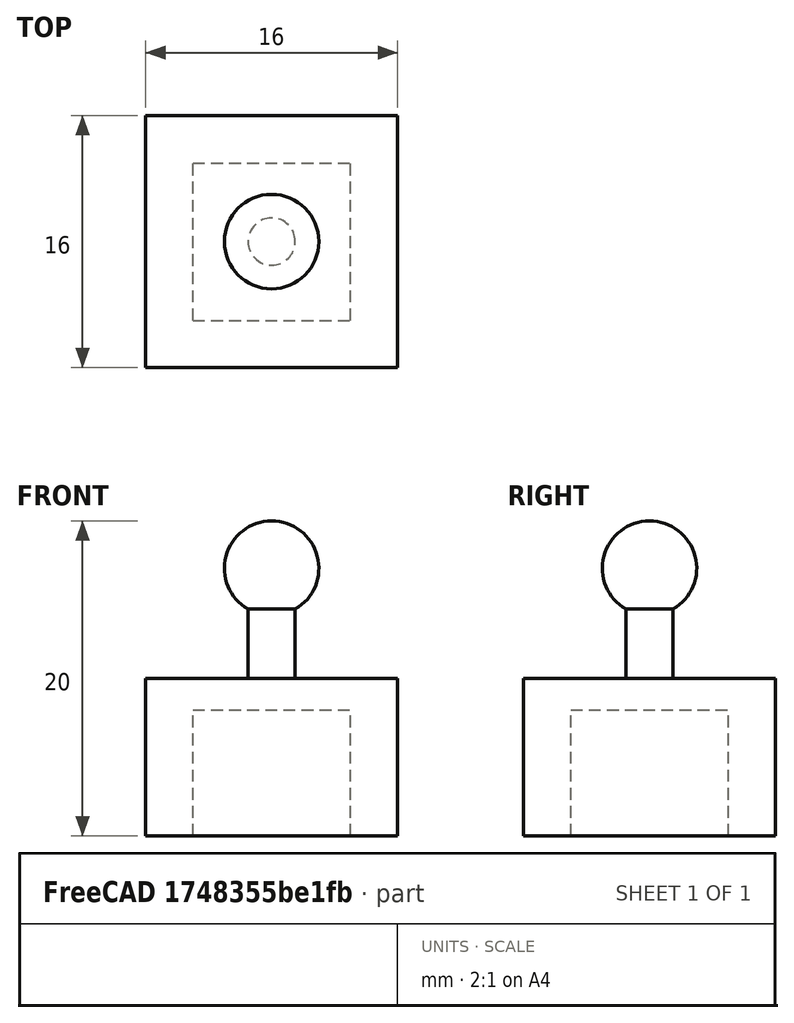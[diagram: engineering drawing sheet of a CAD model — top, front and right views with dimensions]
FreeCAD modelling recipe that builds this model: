
FCSTD DOCUMENT  (FreeCAD 0.18.3R)
Label: sphere
License: All rights reserved
LicenseURL: http://en.wikipedia.org/wiki/All_rights_reserved
objects: Part::Box×2, Part::Cylinder×1, Part::Sphere×1, Part::MultiFuse×1, Part::Cut×1
note: 6 computed .brp shape members not serialized (recipe doc carries the construction recipe); baked Part::Feature solids carry a one-line shape summary decoded from their .brp

FEATURE [Part::Box] Box  label="Cube"
  AttacherType = Attacher::AttachEngine3D
  Height = 10
  Length = 16
  Placement = pos=(-8,-8,0) rot=(0,0,1;0rad)
  Width = 16
FEATURE [Part::Cylinder] Cylinder
  Angle = 360
  AttacherType = Attacher::AttachEngine3D
  Height = 5
  Placement = pos=(0,0,10) rot=(0,0,1;0rad)
  Radius = 1.5
FEATURE [Part::Sphere] Sphere
  Angle1 = -90
  Angle2 = 90
  Angle3 = 360
  AttacherType = Attacher::AttachEngine3D
  Placement = pos=(0,0,17) rot=(0,0,1;0rad)
  Radius = 3
FEATURE [Part::MultiFuse] Fusion
  Shapes = -> [Box,Cylinder,Sphere]
FEATURE [Part::Box] Box001  label="Cube001"
  AttacherType = Attacher::AttachEngine3D
  Height = 8
  Length = 10
  Placement = pos=(-5,-5,0) rot=(0,0,1;0rad)
  Width = 10
FEATURE [Part::Cut] Cut
  Base = -> Fusion
  Tool = -> Box001
